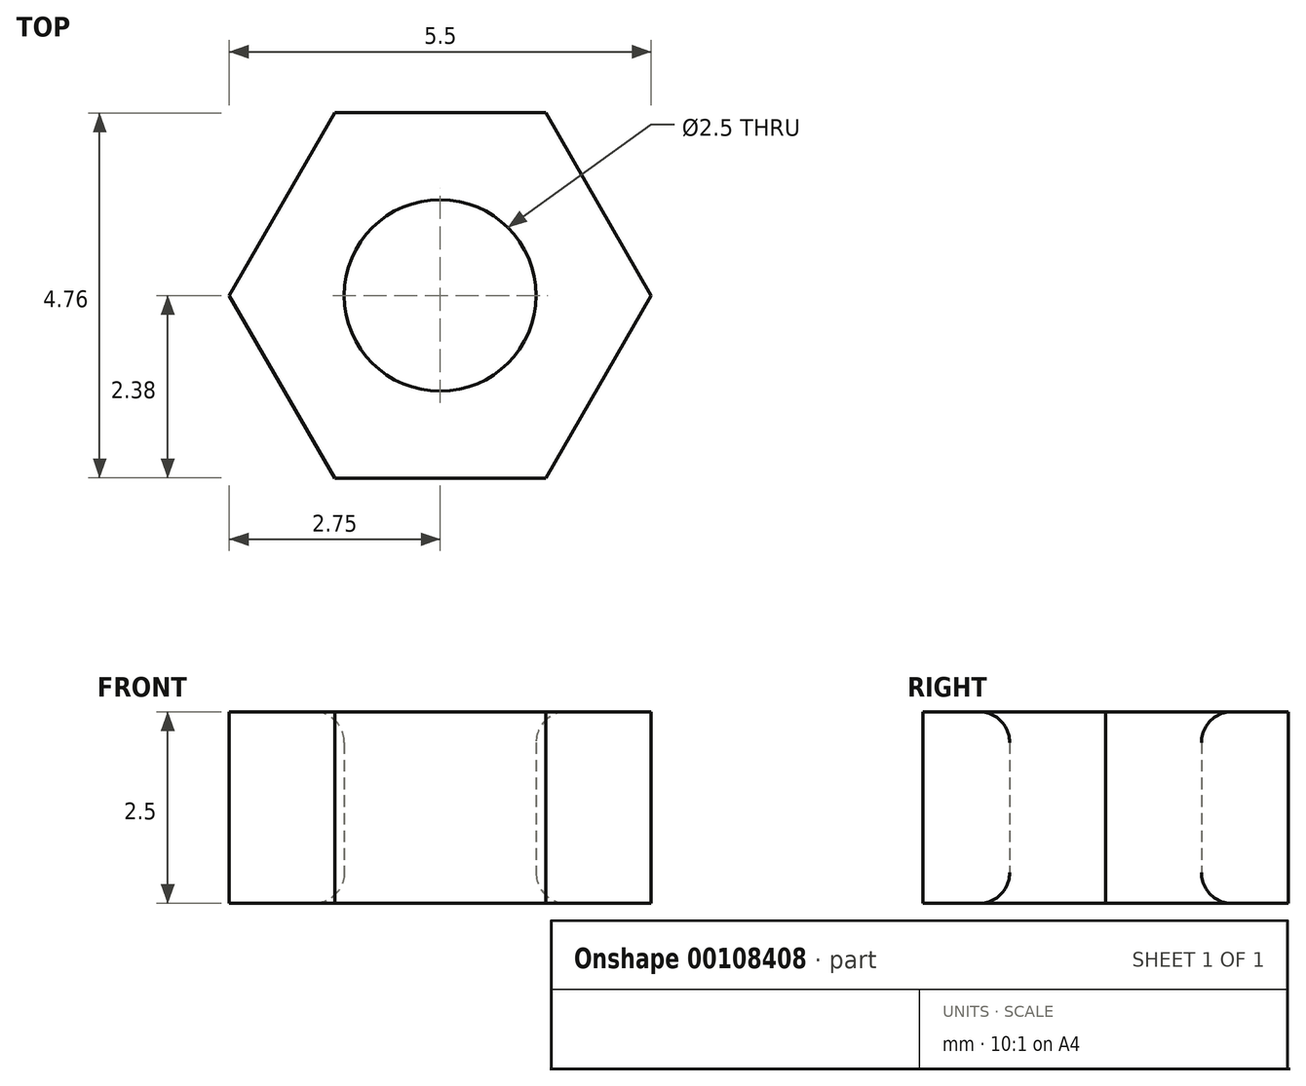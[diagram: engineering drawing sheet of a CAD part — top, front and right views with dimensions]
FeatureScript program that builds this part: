
annotation { "Feature Type Name" : "Feature", "Feature Type Description" : "" }
export const myFeature = defineFeature(function(context is Context, id is Id, definition is map)
    precondition{}
    {
        {
            var Q0;
            Q0=qCreatedBy(makeId("Top.planeOp"),FACE);
            var sketch = newSketch(context, id + "F0", { "sketchPlane" : qUnion([Q0])});
            skCircle(sketch, "E0", {"center": v(0, 0) * mm, "radius": 1.25 * mm});
            skCircle(sketch, "E1.cCircle", {"center": v(0, 0) * mm, "radius": 2.38 * mm, "construction": true});
            skLineSegment(sketch, "E1.0", {"start": v(-1.38, 2.38) * mm, "end": v(1.38, 2.38) * mm});
            skLineSegment(sketch, "E1.1", {"start": v(1.37, 2.38) * mm, "end": v(2.75, 0) * mm});
            skLineSegment(sketch, "E1.2", {"start": v(2.75, 0) * mm, "end": v(1.38, -2.38) * mm});
            skLineSegment(sketch, "E1.3", {"start": v(1.38, -2.38) * mm, "end": v(-1.37, -2.38) * mm});
            skLineSegment(sketch, "E1.4", {"start": v(-1.37, -2.38) * mm, "end": v(-2.75, 0) * mm});
            skLineSegment(sketch, "E1.5", {"start": v(-2.75, 0) * mm, "end": v(-1.38, 2.38) * mm});
            skPoint(sketch, "E1.0.midPoint", {"position": v(0, 2.38) * mm});
            skSolve(sketch);
        }
        {
            var Q0;
            Q0 = qSketchRegion(id + "F0", true);
            extrude(context, id + "F1", {"entities" : qUnion([Q0]), "depth" : 2.5 * mm});
        }
        {
            var Q0;
            Q0=makeQuery(id+"F1.opExtrude","CAP_EDGE",EDGE,{"disambiguationData":[OSD([sQuery(id+"F0.wireOp",EDGE,"E0")])],"isStart":true});
            fillet(context, id + "F2", {"entities" : qUnion([Q0]), "radius" : .4 * mm, "tangentPropagation" : true, "allowEdgeOverflow" : false});
        }
        {
            var Q0;
            Q0=makeQuery(id+"F1.opExtrude","CAP_EDGE",EDGE,{"disambiguationData":[OSD([sQuery(id+"F0.wireOp",EDGE,"E0")])],"isStart":false});
            fillet(context, id + "F3", {"entities" : qUnion([Q0]), "radius" : .4 * mm, "tangentPropagation" : true, "allowEdgeOverflow" : false});
        }
    });
